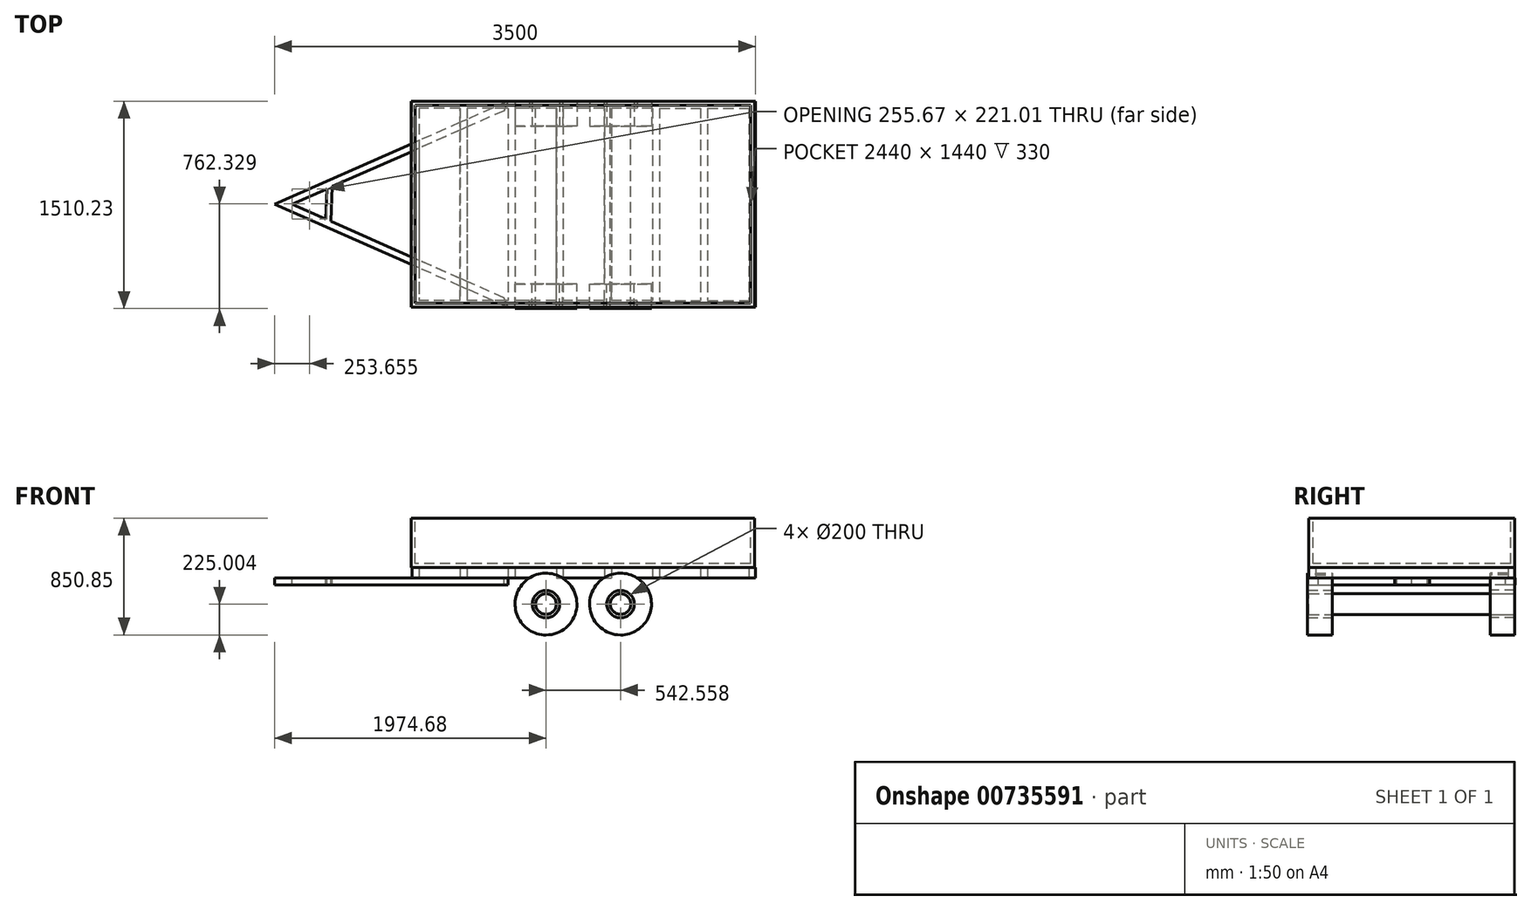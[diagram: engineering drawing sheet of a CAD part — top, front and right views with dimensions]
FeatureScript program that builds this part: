
annotation { "Feature Type Name" : "Feature", "Feature Type Description" : "" }
export const myFeature = defineFeature(function(context is Context, id is Id, definition is map)
    precondition{}
    {
        {
            var Q0;
            Q0=qCreatedBy(makeId("Top.planeOp"),FACE);
            var sketch = newSketch(context, id + "F0", { "sketchPlane" : qUnion([Q0])});
            skLineSegment(sketch, "E0.bottom", {"start": v(1069.78, 749.77) * mm, "end": v(-1430.22, 749.77) * mm});
            skLineSegment(sketch, "E0.top", {"start": v(1069.78, -750.23) * mm, "end": v(-1430.22, -750.23) * mm});
            skLineSegment(sketch, "E0.left", {"start": v(1069.78, 749.77) * mm, "end": v(1069.78, -750.23) * mm});
            skLineSegment(sketch, "E0.right", {"start": v(-1430.22, 749.77) * mm, "end": v(-1430.22, -750.23) * mm});
            skLineSegment(sketch, "E1.0", {"start": v(-1380.22, 699.77) * mm, "end": v(-1380.22, -700.23) * mm});
            skLineSegment(sketch, "E2.left", {"start": v(-1080.22, 699.77) * mm, "end": v(-1080.22, -700.23) * mm});
            skLineSegment(sketch, "E3.trimOffspring", {"start": v(-1080.22, 699.77) * mm, "end": v(-1380.22, 699.77) * mm});
            skLineSegment(sketch, "E4.trimOffspring", {"start": v(-1080.22, -700.23) * mm, "end": v(-1380.22, -700.23) * mm});
            skLineSegment(sketch, "E5.1.0.0", {"start": v(-730.22, 699.77) * mm, "end": v(-730.22, -700.23) * mm});
            skLineSegment(sketch, "E5.1.0.1", {"start": v(-730.22, 699.77) * mm, "end": v(-1030.22, 699.77) * mm});
            skLineSegment(sketch, "E5.1.0.2", {"start": v(-1030.22, 699.77) * mm, "end": v(-1030.22, -700.23) * mm});
            skLineSegment(sketch, "E5.1.0.3", {"start": v(-730.22, -700.23) * mm, "end": v(-1030.22, -700.23) * mm});
            skLineSegment(sketch, "E5.2.0.0", {"start": v(-380.22, 699.77) * mm, "end": v(-380.22, -700.23) * mm});
            skLineSegment(sketch, "E5.2.0.1", {"start": v(-380.22, 699.77) * mm, "end": v(-680.22, 699.77) * mm});
            skLineSegment(sketch, "E5.2.0.2", {"start": v(-680.22, 699.77) * mm, "end": v(-680.22, -700.23) * mm});
            skLineSegment(sketch, "E5.2.0.3", {"start": v(-380.22, -700.23) * mm, "end": v(-680.22, -700.23) * mm});
            skLineSegment(sketch, "E5.3.0.0", {"start": v(-30.22, 699.77) * mm, "end": v(-30.22, -700.23) * mm});
            skLineSegment(sketch, "E5.3.0.1", {"start": v(-30.22, 699.77) * mm, "end": v(-330.22, 699.77) * mm});
            skLineSegment(sketch, "E5.3.0.2", {"start": v(-330.22, 699.77) * mm, "end": v(-330.22, -700.23) * mm});
            skLineSegment(sketch, "E5.3.0.3", {"start": v(-30.22, -700.23) * mm, "end": v(-330.22, -700.23) * mm});
            skLineSegment(sketch, "E5.4.0.0", {"start": v(319.78, 699.77) * mm, "end": v(319.78, -700.23) * mm});
            skLineSegment(sketch, "E5.4.0.1", {"start": v(319.78, 699.77) * mm, "end": v(19.78, 699.77) * mm});
            skLineSegment(sketch, "E5.4.0.2", {"start": v(19.78, 699.77) * mm, "end": v(19.78, -700.23) * mm});
            skLineSegment(sketch, "E5.4.0.3", {"start": v(319.78, -700.23) * mm, "end": v(19.78, -700.23) * mm});
            skLineSegment(sketch, "E5.direction1", {"start": v(-1080.22, -700.23) * mm, "end": v(-730.22, -700.23) * mm, "construction": true});
            skLineSegment(sketch, "E6.bottom", {"start": v(369.78, 699.77) * mm, "end": v(669.78, 699.77) * mm});
            skLineSegment(sketch, "E6.top", {"start": v(369.78, -700.23) * mm, "end": v(669.78, -700.23) * mm});
            skLineSegment(sketch, "E6.left", {"start": v(369.78, 699.77) * mm, "end": v(369.78, -700.23) * mm});
            skLineSegment(sketch, "E6.right", {"start": v(669.78, 699.77) * mm, "end": v(669.78, -700.23) * mm});
            skLineSegment(sketch, "E7.bottom", {"start": v(719.78, 699.77) * mm, "end": v(1019.78, 699.77) * mm});
            skLineSegment(sketch, "E7.top", {"start": v(719.78, -700.23) * mm, "end": v(1019.78, -700.23) * mm});
            skLineSegment(sketch, "E7.left", {"start": v(719.78, 699.77) * mm, "end": v(719.78, -700.23) * mm});
            skLineSegment(sketch, "E7.right", {"start": v(1019.78, 699.77) * mm, "end": v(1019.78, -700.23) * mm});
            skSolve(sketch);
        }
        {
            var Q0;
            Q0=qSketchRegion(id+"F0",true);
            var Q1;
            Q1=qSketchRegion(id+"F2",true);
            extrude(context, id + "F1", {"entities" : qUnion([Q0, Q1]), "depth" : 76.2 * mm});
        }
        {
            var Q0;
            Q0=makeQuery(id+"F1.opExtrude","CAP_FACE",FACE,{"disambiguationData":[OSD([sQuery(id+"F0.wireOp",EDGE,"E0.bottom"),sQuery(id+"F0.wireOp",EDGE,"E0.top"),sQuery(id+"F0.wireOp",EDGE,"E0.left"),sQuery(id+"F0.wireOp",EDGE,"E0.right"),sQuery(id+"F0.wireOp",EDGE,"E1.0"),sQuery(id+"F0.wireOp",EDGE,"E2.left"),sQuery(id+"F0.wireOp",EDGE,"E3.trimOffspring"),sQuery(id+"F0.wireOp",EDGE,"E4.trimOffspring"),sQuery(id+"F0.wireOp",EDGE,"E5.1.0.0"),sQuery(id+"F0.wireOp",EDGE,"E5.1.0.1"),sQuery(id+"F0.wireOp",EDGE,"E5.1.0.2"),sQuery(id+"F0.wireOp",EDGE,"E5.1.0.3"),sQuery(id+"F0.wireOp",EDGE,"E5.2.0.0"),sQuery(id+"F0.wireOp",EDGE,"E5.2.0.1"),sQuery(id+"F0.wireOp",EDGE,"E5.2.0.2"),sQuery(id+"F0.wireOp",EDGE,"E5.2.0.3"),sQuery(id+"F0.wireOp",EDGE,"E5.3.0.0"),sQuery(id+"F0.wireOp",EDGE,"E5.3.0.1"),sQuery(id+"F0.wireOp",EDGE,"E5.3.0.2"),sQuery(id+"F0.wireOp",EDGE,"E5.3.0.3"),sQuery(id+"F0.wireOp",EDGE,"E5.4.0.0"),sQuery(id+"F0.wireOp",EDGE,"E5.4.0.1"),sQuery(id+"F0.wireOp",EDGE,"E5.4.0.2"),sQuery(id+"F0.wireOp",EDGE,"E5.4.0.3")])],"isStart":true});
            var sketch = newSketch(context, id + "F2", { "sketchPlane" : qUnion([Q0])});
            skLineSegment(sketch, "E8", {"start": v(-730.22, 750.23) * mm, "end": v(-2430.22, 0) * mm});
            skLineSegment(sketch, "E9.0", {"start": v(-761.7, 680.81) * mm, "end": v(-2021.93, 124.66) * mm});
            skLineSegment(sketch, "E10", {"start": v(-730.22, 750.23) * mm, "end": v(-761.7, 680.81) * mm});
            skLineSegment(sketch, "E11", {"start": v(1069.78, 0) * mm, "end": v(-2619.5, 0) * mm, "construction": true});
            skLineSegment(sketch, "E12.0.MirrorCS", {"start": v(-730.22, -750.23) * mm, "end": v(-761.7, -680.81) * mm});
            skLineSegment(sketch, "E12.1.MirrorCS", {"start": v(-761.7, -680.81) * mm, "end": v(-2009.76, -130.03) * mm});
            skLineSegment(sketch, "E12.2.MirrorCS", {"start": v(-730.22, -750.23) * mm, "end": v(-2430.22, 0) * mm});
            skPoint(sketch, "E13.orphan", {"position": v(-2224.3, -35.35) * mm});
            skPoint(sketch, "E14.orphan", {"position": v(-2224.3, 35.35) * mm});
            skLineSegment(sketch, "E15.left", {"start": v(-2059.28, 108.17) * mm, "end": v(-2048.73, -112.83) * mm});
            skLineSegment(sketch, "E15.right", {"start": v(-2021.93, 124.66) * mm, "end": v(-2009.76, -130.03) * mm});
            skLineSegment(sketch, "E16.trimOffspring", {"start": v(-2048.73, -112.83) * mm, "end": v(-2304.4, 0) * mm});
            skLineSegment(sketch, "E17.trimOffspring", {"start": v(-2059.28, 108.17) * mm, "end": v(-2304.4, 0) * mm});
            skSolve(sketch);
        }
        {
            var Q0;
            Q0=qSketchRegion(id+"F2",true);
            extrude(context, id + "F3", {"entities" : qUnion([Q0]), "operationType" : NewBodyOperationType.ADD, "depth" : 50.8 * mm});
        }
        {
            var Q0;
            Q0=qCreatedBy(makeId("Front.planeOp"),FACE);
            var sketch = newSketch(context, id + "F4", { "sketchPlane" : qUnion([Q0])});
            skLineSegment(sketch, "E18.bottom", {"start": v(-1437.5, 76.2) * mm, "end": v(1062.5, 76.2) * mm});
            skLineSegment(sketch, "E18.top", {"start": v(-1437.5, 436.2) * mm, "end": v(1062.5, 436.2) * mm});
            skLineSegment(sketch, "E18.left", {"start": v(-1437.5, 76.2) * mm, "end": v(-1437.5, 436.2) * mm});
            skLineSegment(sketch, "E18.right", {"start": v(1062.5, 76.2) * mm, "end": v(1062.5, 436.2) * mm});
            skSolve(sketch);
        }
        {
            var Q0;
            Q0=makeQuery(id+"F4.imprint","IMPRINT",FACE,{"disambiguationData":[TD([[makeQuery(id+"F4.imprint","IMPRINT",EDGE,{"derivedFrom":sQuery(id+"F4.wireOp",EDGE,"E18.bottom")}),1.0]])]});
            extrude(context, id + "F5", {"entities" : qUnion([Q0]), "operationType" : NewBodyOperationType.ADD, "endBound" : BoundingType.SYMMETRIC, "oppositeDirection" : true, "depth" : 1500 * mm});
        }
        {
            var Q0;
            Q0=makeQuery(id+"F5.opExtrude","SWEPT_FACE",FACE,{"disambiguationData":[OSD([sQuery(id+"F4.wireOp",EDGE,"E18.top")])]});
            shell(context, id + "F6", {"entities" : qUnion([Q0]), "thickness" : 30 * mm});
        }
        {
            var Q0;
            Q0=qCreatedBy(makeId("Front.planeOp"),FACE);
            var sketch = newSketch(context, id + "F7", { "sketchPlane" : qUnion([Q0])});
            skCircle(sketch, "E19", {"center": v(-455.54, -189.65) * mm, "radius": 225 * mm});
            skCircle(sketch, "E20", {"center": v(87.02, -189.65) * mm, "radius": 225 * mm});
            skCircle(sketch, "E21", {"center": v(-455.54, -189.65) * mm, "radius": 100 * mm});
            skCircle(sketch, "E22", {"center": v(87.02, -189.65) * mm, "radius": 100 * mm});
            skSolve(sketch);
        }
        {
            var Q0;
            Q0=makeQuery(id+"F7.imprint","IMPRINT",FACE,{"disambiguationData":[TD([[makeQuery(id+"F7.imprint","IMPRINT",EDGE,{"derivedFrom":sQuery(id+"F7.wireOp",EDGE,"E19")}),1.0]])]});
            var Q1;
            Q1=makeQuery(id+"F7.imprint","IMPRINT",FACE,{"disambiguationData":[TD([[makeQuery(id+"F7.imprint","IMPRINT",EDGE,{"derivedFrom":sQuery(id+"F7.wireOp",EDGE,"E20")}),1.0]])]});
            extrude(context, id + "F8", {"entities" : qUnion([Q0, Q1]), "operationType" : NewBodyOperationType.ADD, "oppositeDirection" : true, "depth" : 750 * mm, "hasSecondDirection" : true, "secondDirectionOppositeDirection" : true, "secondDirectionDepth" : 570 * mm});
        }
        {
            var Q0;
            Q0=qSketchRegion(id+"F7",true);
            extrude(context, id + "F9", {"entities" : qUnion([Q0]), "operationType" : NewBodyOperationType.ADD, "depth" : 760 * mm, "hasSecondDirection" : true, "secondDirectionOppositeDirection" : false, "secondDirectionDepth" : 580 * mm});
        }
        {
            var Q0;
            Q0=qCreatedBy(makeId("Front.planeOp"),FACE);
            var sketch = newSketch(context, id + "F10", { "sketchPlane" : qUnion([Q0])});
            skCircle(sketch, "E23", {"center": v(-455.54, -189.65) * mm, "radius": 75 * mm});
            skCircle(sketch, "E24", {"center": v(87.02, -189.65) * mm, "radius": 75 * mm});
            skSolve(sketch);
        }
        {
            var Q0;
            Q0=qSketchRegion(id+"F10",true);
            extrude(context, id + "F11", {"entities" : qUnion([Q0]), "depth" : 750 * mm, "hasSecondDirection" : true, "secondDirectionOppositeDirection" : true, "secondDirectionDepth" : 750 * mm});
        }
    });
